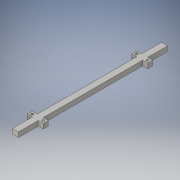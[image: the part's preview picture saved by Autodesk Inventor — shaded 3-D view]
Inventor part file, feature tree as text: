
AUTODESK INVENTOR PART (.ipt)
format: ipt  version: 2016 (Build 200138000, 138)  size: 125,440 bytes
history: native  units: in
note: dims shown in document units (in); Inventor stores cm internally (conversion verified against a paired STEP export)
features: extrude x2, mirror x2, sketch x2
ambient origin geometry x8: Origin, YZ Plane, XZ Plane, XY Plane, X Axis, Y Axis, Z Axis, Center Point
bodies: Solid1 (feature_tree)
feature tree (6):
  extrude  "Extrusion1"  Depth=15.0in
  extrude  "Extrusion2"  Depth=0.5in
  mirror  "Mirror1"
  mirror  "Mirror2"
  sketch  "Sketch1"  dims[d0=0.6in d1=15.0in]
  sketch  "Sketch2"  dims[d2=0.5in d3=0.0in d4=0.5in d5=0.5in d6=5.0in d7=0.25in d8=0.25in d9=0.25in d10=0.5in d11=0.0in]
